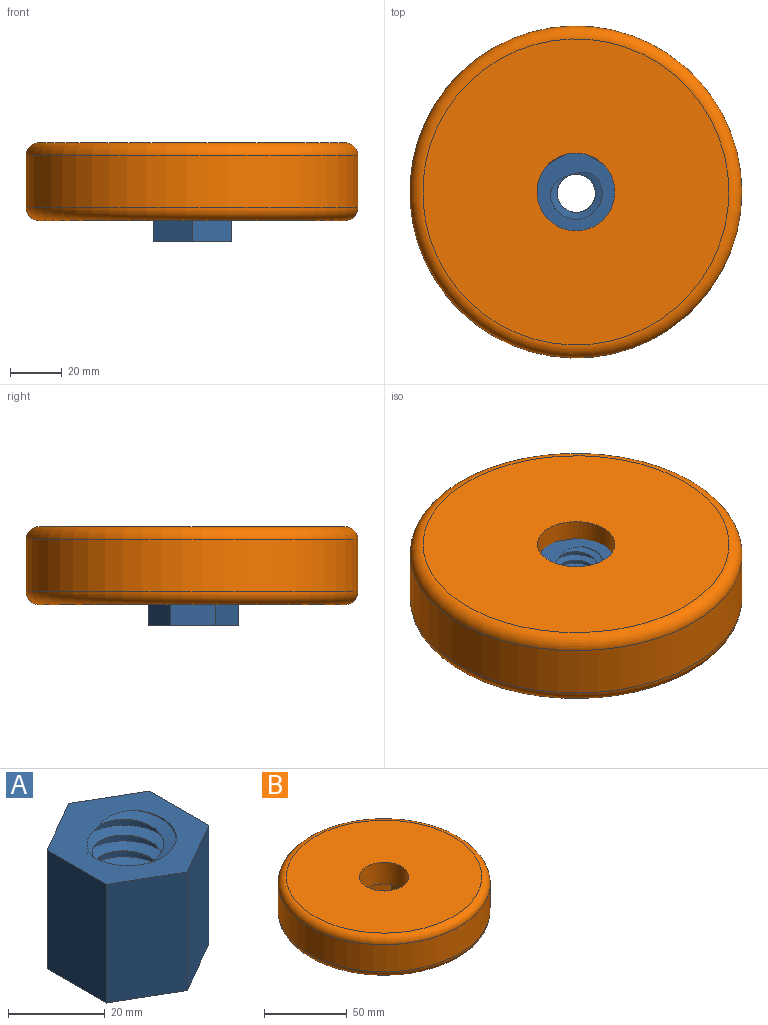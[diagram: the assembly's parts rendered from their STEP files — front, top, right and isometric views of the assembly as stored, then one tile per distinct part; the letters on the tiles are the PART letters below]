
ASSEMBLY  parts=2 mates=1
PART A: 12 faces, bbox 30x34.6x32.7 mm
  f0: plane 30x17.32mm, normal (1,0,0), area 519.6mm2, adj f1,f5,f6,f7
  f1: plane 30x15mm, normal (0.5,0.87,0), area 519.6mm2, adj f0,f2,f6,f7
  f2: plane 30x15mm, normal (-0.5,0.87,0), area 519.6mm2, adj f1,f3,f6,f7
  f3: plane 30x17.32mm, normal (-1,0,0), area 519.6mm2, adj f2,f4,f6,f7
  f4: plane 30x15mm, normal (-0.5,-0.87,0), area 519.6mm2, adj f3,f5,f6,f7
  f5: plane 30x15mm, normal (0.5,-0.87,0), area 519.6mm2, adj f0,f4,f6,f7
  f6: plane 34.64x30mm, normal (0,0,1), area 498.6mm2, adj f0,f1,f2,f3,f4,f5,f8,f9
  f7: plane 34.64x30mm, normal (0,0,-1), area 498.6mm2, adj f0,f1,f2,f3,f4,f5,f8,f9
  f8: cylinder r=7.4mm len=30mm, axis (0,0,-1), area -43.8mm2, adj f6,f7,f9,f10
  f9: bspline ~32.03x23.09mm, area 1102.6mm2, adj f6,f7,f8,f11
  f10: bspline ~32.7x23.09mm, area 1111.9mm2, adj f6,f7,f8,f11
  f11: cylinder r=10mm len=30mm, axis (0,0,-1), area 1322.8mm2, adj f6,f7,f9,f10
PART B: 18 faces, bbox 138.5x138.5x30 mm
  f0: cylinder r=15mm len=30mm, axis (0,0,-1), area 1508mm2, adj f2,f12,f13,f14,f15,f16,f17
  f1: cylinder r=64mm len=128mm, axis (0,0,-1), area 8042.5mm2, adj f4,f5
  f2: plane 118x118mm, normal (0,0,1), area 10229mm2, adj f0,f5
  f3: plane 118x118mm, normal (0,0,-1), area 10156.5mm2, adj f4,f6,f7,f8,f9,f10,f11
  f4: torus R=59mm, axis (0,0,1), area 3068.6mm2, adj f1,f3
  f5: torus R=59mm, axis (0,0,1), area 3068.6mm2, adj f1,f2
  f6: plane 17.32x14mm, normal (1,0,0), area 242.5mm2, adj f3,f7,f11,f12,f17
  f7: plane 15x14mm, normal (0.5,-0.87,0), area 242.5mm2, adj f3,f6,f8,f12,f13
  f8: plane 15x14mm, normal (-0.5,-0.87,0), area 242.5mm2, adj f3,f7,f9,f13,f14
  f9: plane 17.32x14mm, normal (-1,0,0), area 242.5mm2, adj f3,f8,f10,f14,f15
  f10: plane 15x14mm, normal (-0.5,0.87,0), area 242.5mm2, adj f3,f9,f11,f15,f16
  f11: plane 15x14mm, normal (0.5,0.87,0), area 242.5mm2, adj f3,f6,f10,f16,f17
  f12: plane 12.99x7.5mm, normal (0,0,-1), area 12.1mm2, adj f0,f6,f7
  f13: plane 15x4.33mm, normal (0,0,-1), area 12.1mm2, adj f0,f7,f8
  f14: plane 12.99x7.5mm, normal (0,0,-1), area 12.1mm2, adj f0,f8,f9
  f15: plane 12.99x7.5mm, normal (0,0,-1), area 12.1mm2, adj f0,f9,f10
  f16: plane 15x4.33mm, normal (0,0,-1), area 12.1mm2, adj f0,f10,f11
  f17: plane 12.99x7.5mm, normal (0,0,-1), area 12.1mm2, adj f0,f6,f11
PLACE A t=(13.39,54.05,47.37)mm
PLACE B t=(13.23,54.55,55.37)mm
MATE fastened A.f6 <-> B.f0  axis (0,0,1) through (13.23,54.55,77.37)mm
